# Revit family: good-2015_Valvula_Valvulas-Arco_Tajo
name_source: partatom
category: Pipe Accessories
revit_build: Autodesk Revit 2015 (Build: 20140223_1515(x64)
units: mm (PartAtom-declared; Revit-internal decimal feet)

## types (11) — shared parameters
Acabado = Cromado
Autor = Bimetica PDS
B Ancho = 22.000 mm
COBieCategoria = IfcValve
ClasificacionDeCierre = 0.00 bar
CodigoGubimclass = 50.10.20.10
DescripcionGubimclass = Válvulas e instrumentos de medida y control de flujo de fontanería
Description = Válvula esfera Turia mando palanca H-H
FechaEmisionElementoBIM = 11/02/2020
FechaVencimientoElementoBIM = 11/02/2021
GarantiaExtendida = Yes
Historial = (RVT2015-V01) Creación del elemento
IfcExportAs = IfcValve
IfcExportType = Ball Valve
K Coefficient = 0.35
Manufacturer = Vávulas Arco S.L
Marcado CE = Yes
MasterformatCodigo = 35 20 19
MasterformatTitulo = Hydraulic Valves
MaterialCarcasa = Latón Europeo CW617N
MecanismoValvula = BALL
Model = Tajo
Numero de Licencia = XXX-XXXX9536
OmniclassCodigo = 23-27 31 15
OmniclassTitulo = Ball Valves
OperacionValvula = PALANCA
PatronValvula = STRAIGHT_2_PORT
PresionDePrueba = 0.00 bar
PresionDeTrabajo = 0.00 bar
PresionNominal = 5.00 bar
Sistema = Agua potable, agua caliente sanitaria y aire comprimido
TelefonoContacto = 0034 963 17 10 70
TemperaturaMaxima = 140 °C
TemprerturaMinima = -20 °C
Titular = Vávulas Arco S.L
Type Comments = Agua potable, agua caliente sanitaria y aire comprimido
UNSPSCCodigo = 40141607
UNSPSCTitulo = Ball valves
URLPerfilProductoBimetica = https://bimetica.com
Uniclass2015Codigo = 65-54-95-13
Uniclass2015Titulo = Check valves
Version = RVT2015
zero-valued in all types: AcidificacionAtmosfericaPorUnidad, AguaConsumidaPorUnidad, CambioClimaticoPorUnidad, CosteMantenimiento, CurvaSonido, DestruccionCapaOzonoEstratosfericaPorUnidad, Energia consumida, EnergiaNoRenovableConsumidaPorUnidad, EnergiaPrimariaTotalConsumidaPorUnidad, EnergiaRenovableConsumidaPorUnidad, EutrofizacionPorUnidad, FaltaDeRecursosPorUnidad, FechaEvaluacion, FormacionFotoquimicaOzonoPorUnidad, ResiduoInertePorUnidad, ResiduoRadioactivoPorUnidad, ResiduosNoPeligrososPorUnidad, ResiduosPeligrososPorUnidad

## per-type parameters (varying)
- 1/4H x 1/4H: A=44.000 mm; Altura Cuerpo=10.319 mm; B=68.000 mm; Basico=Yes; C=40.000 mm; C Diametro=8.000 mm; C Radio=4.000 mm; Codigo=00003; CoeficienteDeCaudal=0; Cost=8.20€; Cuerpo Diametro=7.938 mm; Cuerpo Longitud=11.000 mm; Cuerpo Radio=3.969 mm; D=0"; D Radio=0"; E=0"; E Radio=0"; Longitud=22.000 mm; Longitud 1=11.000 mm; Normal=No; R=0"; Radio=0.318 mm; Referencia=00003; Rosca Ancho=11.000 mm; Rosca Diametro=8.890 mm; Rosca Radio=4.445 mm; Tamano=0"; Tuerca Altura=2.381 mm; Tuerca Diametro=2.540 mm; Tuerca Radio=1.270 mm
- 3/8H x 3/8H: A=44.000 mm; Altura Cuerpo=15.478 mm; B=68.000 mm; Basico=Yes; C=40.000 mm; C Diametro=8.000 mm; C Radio=4.000 mm; Codigo=00004; CoeficienteDeCaudal=0; Cost=8.20€; Cuerpo Diametro=11.906 mm; Cuerpo Longitud=11.000 mm; Cuerpo Radio=5.953 mm; D=0"; D Radio=0"; E=0"; E Radio=0"; Longitud=22.000 mm; Longitud 1=11.000 mm; Normal=No; R=0"; Radio=0.476 mm; Referencia=00004; Rosca Ancho=11.000 mm; Rosca Diametro=13.335 mm; Rosca Radio=6.668 mm; Tamano=0"; Tuerca Altura=3.572 mm; Tuerca Diametro=3.810 mm; Tuerca Radio=1.905 mm
- 1/2H x 1/2H: A=60.000 mm; Altura Cuerpo=20.638 mm; B=93.000 mm; Basico=Yes; C=62.000 mm; C Diametro=12.400 mm; C Radio=6.200 mm; Codigo=00005; CoeficienteDeCaudal=16.1; Cost=8.82€; Cuerpo Diametro=15.875 mm; Cuerpo Longitud=15.000 mm; Cuerpo Radio=7.938 mm; D=1"; D Radio=0"; E=1"; E Radio=0"; Longitud=30.000 mm; Longitud 1=15.000 mm; Normal=No; R=0"; Radio=0.635 mm; Referencia=00005; Rosca Ancho=15.000 mm; Rosca Diametro=17.780 mm; Rosca Radio=8.890 mm; Tamano=1"; Tuerca Altura=4.763 mm; Tuerca Diametro=5.080 mm; Tuerca Radio=2.540 mm
- 3/4H x 3/4H: A=66.000 mm; Altura Cuerpo=30.956 mm; B=93.000 mm; Basico=No; C=70.000 mm; C Diametro=14.000 mm; C Radio=7.000 mm; Codigo=00006; CoeficienteDeCaudal=23.2; Cost=12.72€; Cuerpo Diametro=23.813 mm; Cuerpo Longitud=16.500 mm; Cuerpo Radio=11.906 mm; D=1"; D Radio=0"; E=1"; E Radio=0"; Longitud=33.000 mm; Longitud 1=16.500 mm; Normal=Yes; R=0"; Radio=0.953 mm; Referencia=00006; Rosca Ancho=16.500 mm; Rosca Diametro=26.670 mm; Rosca Radio=13.335 mm; Tamano=1"; Tuerca Altura=7.144 mm; Tuerca Diametro=7.620 mm; Tuerca Radio=3.810 mm
- 1H x 1H: A=80.000 mm; Altura Cuerpo=41.275 mm; B=112.000 mm; Basico=No; C=81.000 mm; C Diametro=16.200 mm; C Radio=8.100 mm; Codigo=00007; CoeficienteDeCaudal=45.8; Cost=19.10€; Cuerpo Diametro=31.750 mm; Cuerpo Longitud=20.000 mm; Cuerpo Radio=15.875 mm; D=1"; D Radio=1"; E=1"; E Radio=1"; Longitud=40.000 mm; Longitud 1=20.000 mm; Normal=Yes; R=1"; Radio=1.270 mm; Referencia=00007; Rosca Ancho=20.000 mm; Rosca Diametro=35.560 mm; Rosca Radio=17.780 mm; Tamano=1"; Tuerca Altura=9.525 mm; Tuerca Diametro=10.160 mm; Tuerca Radio=5.080 mm
- 1-1/4H x 1-1/4H: A=89.000 mm; Altura Cuerpo=51.594 mm; B=112.000 mm; Basico=No; C=90.000 mm; C Diametro=18.000 mm; C Radio=9.000 mm; Codigo=00008; CoeficienteDeCaudal=65.7; Cost=29.25€; Cuerpo Diametro=39.688 mm; Cuerpo Longitud=22.250 mm; Cuerpo Radio=19.844 mm; D=1"; D Radio=1"; E=1"; E Radio=1"; Longitud=44.500 mm; Longitud 1=22.250 mm; Normal=Yes; R=1"; Radio=1.588 mm; Referencia=00008; Rosca Ancho=22.250 mm; Rosca Diametro=44.450 mm; Rosca Radio=22.225 mm; Tamano=1"; Tuerca Altura=11.906 mm; Tuerca Diametro=12.700 mm; Tuerca Radio=6.350 mm
- 1-1/2H x 1-1/2H: A=108.000 mm; Altura Cuerpo=61.913 mm; B=152.000 mm; Basico=No; C=107.000 mm; C Diametro=21.400 mm; C Radio=10.700 mm; Codigo=00009; CoeficienteDeCaudal=113.2; Cost=45.62€; Cuerpo Diametro=47.625 mm; Cuerpo Longitud=27.000 mm; Cuerpo Radio=23.813 mm; D=2"; D Radio=1"; E=2"; E Radio=1"; Longitud=54.000 mm; Longitud 1=27.000 mm; Normal=Yes; R=1"; Radio=1.905 mm; Referencia=00009; Rosca Ancho=27.000 mm; Rosca Diametro=53.340 mm; Rosca Radio=26.670 mm; Tamano=2"; Tuerca Altura=14.288 mm; Tuerca Diametro=15.240 mm; Tuerca Radio=7.620 mm
- 2H x 2H: A=125.000 mm; Altura Cuerpo=82.550 mm; B=152.000 mm; Basico=No; C=127.000 mm; C Diametro=25.400 mm; C Radio=12.700 mm; Codigo=00010; CoeficienteDeCaudal=138.2; Cost=66.91€; Cuerpo Diametro=63.500 mm; Cuerpo Longitud=31.250 mm; Cuerpo Radio=31.750 mm; D=2"; D Radio=1"; E=2"; E Radio=1"; Longitud=62.500 mm; Longitud 1=31.250 mm; Normal=Yes; R=1"; Radio=2.540 mm; Referencia=00010; Rosca Ancho=31.250 mm; Rosca Diametro=71.120 mm; Rosca Radio=35.560 mm; Tamano=2"; Tuerca Altura=19.050 mm; Tuerca Diametro=20.320 mm; Tuerca Radio=10.160 mm
- 2-1/2H x 2-1/2H: A=150.000 mm; Altura Cuerpo=103.188 mm; B=172.000 mm; Basico=No; C=142.000 mm; C Diametro=28.400 mm; C Radio=14.200 mm; Codigo=00011; CoeficienteDeCaudal=262.4; Cost=114.80€; Cuerpo Diametro=79.375 mm; Cuerpo Longitud=37.500 mm; Cuerpo Radio=39.688 mm; D=3"; D Radio=1"; E=3"; E Radio=1"; Longitud=75.000 mm; Longitud 1=37.500 mm; Normal=Yes; R=1"; Radio=3.175 mm; Referencia=00011; Rosca Ancho=37.500 mm; Rosca Diametro=88.900 mm; Rosca Radio=44.450 mm; Tamano=3"; Tuerca Altura=23.813 mm; Tuerca Diametro=25.400 mm; Tuerca Radio=12.700 mm
- 3H x 3H: A=160.000 mm; Altura Cuerpo=113.506 mm; B=240.000 mm; Basico=No; C=200.000 mm; C Diametro=40.000 mm; C Radio=20.000 mm; Codigo=01109; CoeficienteDeCaudal=418.6; Cost=185.39€; Cuerpo Diametro=87.313 mm; Cuerpo Longitud=40.000 mm; Cuerpo Radio=43.656 mm; D=3"; D Radio=1"; E=3"; E Radio=1"; Longitud=80.000 mm; Longitud 1=40.000 mm; Normal=Yes; R=2"; Radio=3.493 mm; Referencia=01109; Rosca Ancho=40.000 mm; Rosca Diametro=97.790 mm; Rosca Radio=48.895 mm; Tamano=3"; Tuerca Altura=26.194 mm; Tuerca Diametro=27.940 mm; Tuerca Radio=13.970 mm
- 4H x 4H: A=190.000 mm; Altura Cuerpo=165.100 mm; B=240.000 mm; Basico=No; C=215.000 mm; C Diametro=43.000 mm; C Radio=21.500 mm; Codigo=01110; CoeficienteDeCaudal=851.3; Cost=331.82€; Cuerpo Diametro=127.000 mm; Cuerpo Longitud=47.500 mm; Cuerpo Radio=63.500 mm; D=4"; D Radio=2"; E=4"; E Radio=2"; Longitud=95.000 mm; Longitud 1=47.500 mm; Normal=Yes; R=2"; Radio=5.080 mm; Referencia=01110; Rosca Ancho=47.500 mm; Rosca Diametro=142.240 mm; Rosca Radio=71.120 mm; Tamano=4"; Tuerca Altura=38.100 mm; Tuerca Diametro=40.640 mm; Tuerca Radio=20.320 mm

## geometry (parser evidence)
native form markers: Sweep x2
no freeform markers — native parametric forms only
